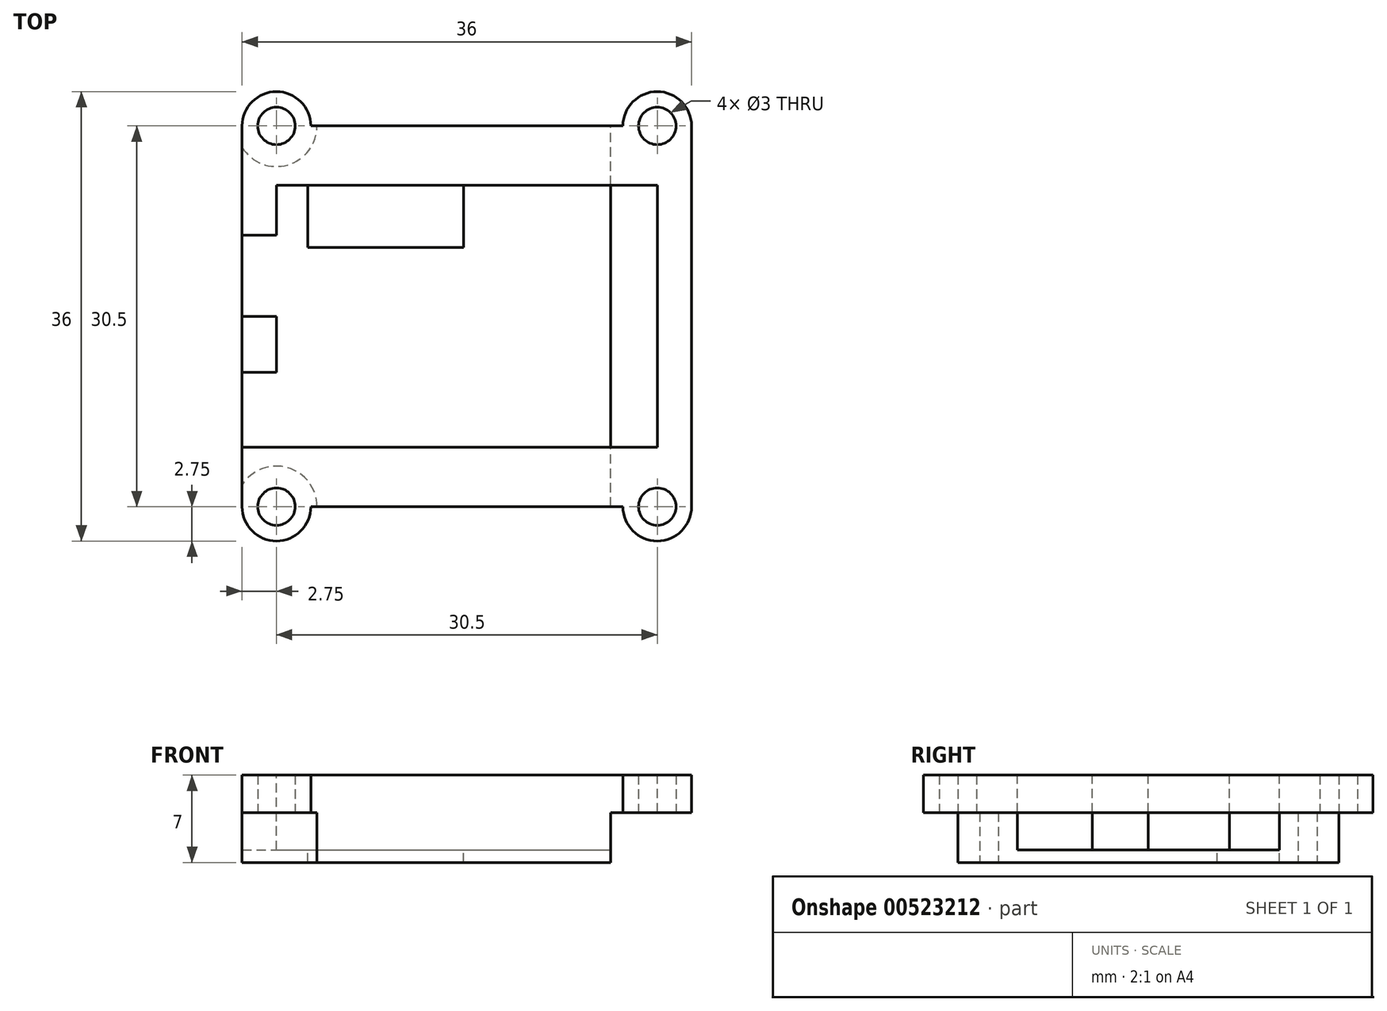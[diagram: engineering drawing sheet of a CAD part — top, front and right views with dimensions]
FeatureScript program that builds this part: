
annotation { "Feature Type Name" : "Feature", "Feature Type Description" : "" }
export const myFeature = defineFeature(function(context is Context, id is Id, definition is map)
    precondition{}
    {
        {
            var Q0;
            Q0=qCreatedBy(makeId("Top.planeOp"),FACE);
            var sketch = newSketch(context, id + "F0", { "sketchPlane" : qUnion([Q0])});
            skLineSegment(sketch, "E0.bottom", {"start": v(-18, -18) * mm, "end": v(18, -18) * mm});
            skLineSegment(sketch, "E0.top", {"start": v(-18, 18) * mm, "end": v(18, 18) * mm});
            skLineSegment(sketch, "E0.left", {"start": v(-18, -18) * mm, "end": v(-18, 18) * mm});
            skLineSegment(sketch, "E0.right", {"start": v(18, -18) * mm, "end": v(18, 18) * mm});
            skPoint(sketch, "E0.middle", {"position": v(0, 0) * mm});
            skSolve(sketch);
        }
        {
            var Q0;
            Q0=makeQuery(id+"F0.imprint","IMPRINT",FACE,{"disambiguationData":[TD([[makeQuery(id+"F0.imprint","IMPRINT",EDGE,{"derivedFrom":sQuery(id+"F0.wireOp",EDGE,"E0.bottom")}),1.0]])]});
            var Q1;
            Q1 = qSketchRegion(id + "F2", true);
            extrude(context, id + "F1", {"entities" : qUnion([Q0, Q1]), "depth" : 7 * mm, "offsetDistance" : 25 * mm});
        }
        {
            var Q0;
            Q0=makeQuery(id+"F1.opExtrude","CAP_FACE",FACE,{"disambiguationData":[OSD([sQuery(id+"F0.wireOp",EDGE,"E0.bottom"),sQuery(id+"F0.wireOp",EDGE,"E0.top"),sQuery(id+"F0.wireOp",EDGE,"E0.left"),sQuery(id+"F0.wireOp",EDGE,"E0.right")])],"isStart":false});
            var Q1;
            Q1=makeQuery(id+"F1.opExtrude","CAP_FACE",FACE,{"disambiguationData":[OSD([sQuery(id+"F0.wireOp",EDGE,"E0.bottom"),sQuery(id+"F0.wireOp",EDGE,"E0.top"),sQuery(id+"F0.wireOp",EDGE,"E0.left"),sQuery(id+"F0.wireOp",EDGE,"E0.right")])],"isStart":false});
            var Q2;
            Q2=makeQuery(id+"F1.opExtrude","CAP_FACE",FACE,{"disambiguationData":[OSD([sQuery(id+"F0.wireOp",EDGE,"E0.bottom"),sQuery(id+"F0.wireOp",EDGE,"E0.top"),sQuery(id+"F0.wireOp",EDGE,"E0.left"),sQuery(id+"F0.wireOp",EDGE,"E0.right")])],"isStart":false});
            var Q3;
            Q3=makeQuery(id+"F1.opExtrude","CAP_FACE",FACE,{"disambiguationData":[OSD([sQuery(id+"F0.wireOp",EDGE,"E0.bottom"),sQuery(id+"F0.wireOp",EDGE,"E0.top"),sQuery(id+"F0.wireOp",EDGE,"E0.left"),sQuery(id+"F0.wireOp",EDGE,"E0.right")])],"isStart":false});
            var Q4;
            Q4=makeQuery(id+"F1.opExtrude","CAP_FACE",FACE,{"disambiguationData":[OSD([sQuery(id+"F0.wireOp",EDGE,"E0.bottom"),sQuery(id+"F0.wireOp",EDGE,"E0.top"),sQuery(id+"F0.wireOp",EDGE,"E0.left"),sQuery(id+"F0.wireOp",EDGE,"E0.right")])],"isStart":false});
            var Q5;
            Q5=makeQuery(id+"F1.opExtrude","CAP_FACE",FACE,{"disambiguationData":[OSD([sQuery(id+"F0.wireOp",EDGE,"E0.bottom"),sQuery(id+"F0.wireOp",EDGE,"E0.top"),sQuery(id+"F0.wireOp",EDGE,"E0.left"),sQuery(id+"F0.wireOp",EDGE,"E0.right")])],"isStart":false});
            var Q6;
            Q6=makeQuery(id+"F1.opExtrude","CAP_FACE",FACE,{"disambiguationData":[OSD([sQuery(id+"F0.wireOp",EDGE,"E0.bottom"),sQuery(id+"F0.wireOp",EDGE,"E0.top"),sQuery(id+"F0.wireOp",EDGE,"E0.left"),sQuery(id+"F0.wireOp",EDGE,"E0.right")])],"isStart":false});
            var Q7;
            Q7=makeQuery(id+"F1.opExtrude","CAP_FACE",FACE,{"disambiguationData":[OSD([sQuery(id+"F0.wireOp",EDGE,"E0.bottom"),sQuery(id+"F0.wireOp",EDGE,"E0.top"),sQuery(id+"F0.wireOp",EDGE,"E0.left"),sQuery(id+"F0.wireOp",EDGE,"E0.right")])],"isStart":false});
            var sketch = newSketch(context, id + "F2", { "sketchPlane" : qUnion([Q0, Q1, Q2, Q3, Q4, Q5, Q6, Q7])});
            skLineSegment(sketch, "E1.bottom", {"start": v(-15.25, -10.5) * mm, "end": v(15.25, -10.5) * mm});
            skLineSegment(sketch, "E1.top", {"start": v(-15.25, 10.5) * mm, "end": v(15.25, 10.5) * mm});
            skLineSegment(sketch, "E1.left", {"start": v(-15.25, -10.5) * mm, "end": v(-15.25, 10.5) * mm});
            skLineSegment(sketch, "E1.right", {"start": v(15.25, -10.5) * mm, "end": v(15.25, 10.5) * mm});
            skPoint(sketch, "E1.middle", {"position": v(0, 0) * mm});
            skSolve(sketch);
        }
        {
            var Q0;
            Q0 = qSketchRegion(id + "F2", true);
            extrude(context, id + "F3", {"entities" : qUnion([Q0]), "operationType" : NewBodyOperationType.REMOVE, "oppositeDirection" : true, "depth" : 6 * mm, "offsetDistance" : 25 * mm});
        }
        {
            var Q0;
            Q0=makeQuery(id+"F2.imprint","IMPRINT",FACE,{"disambiguationData":[TD([[makeQuery(id+"F2.imprint","IMPRINT",EDGE,{"derivedFrom":sQuery(id+"F2.wireOp",EDGE,"E1.bottom")}),-1.0]])]});
            var Q1;
            Q1=makeQuery(id+"F2.imprint","IMPRINT",FACE,{"disambiguationData":[TD([[makeQuery(id+"F2.imprint","IMPRINT",EDGE,{"derivedFrom":sQuery(id+"F2.wireOp",EDGE,"E1.bottom")}),-1.0]])]});
            var sketch = newSketch(context, id + "F4", { "sketchPlane" : qUnion([Q0, Q1])});
            skLineSegment(sketch, "E2.bottom", {"start": v(-15.25, -10.5) * mm, "end": v(-18, -10.5) * mm});
            skLineSegment(sketch, "E2.top", {"start": v(-15.25, -4.5) * mm, "end": v(-18, -4.5) * mm});
            skLineSegment(sketch, "E2.left", {"start": v(-15.25, -10.5) * mm, "end": v(-15.25, -4.5) * mm});
            skLineSegment(sketch, "E2.right", {"start": v(-18, -10.5) * mm, "end": v(-18, -4.5) * mm});
            skSolve(sketch);
        }
        {
            var Q0;
            Q0 = qSketchRegion(id + "F4", true);
            extrude(context, id + "F5", {"entities" : qUnion([Q0]), "operationType" : NewBodyOperationType.REMOVE, "oppositeDirection" : true, "depth" : 6 * mm, "offsetDistance" : 25 * mm});
        }
        {
            var Q0;
            Q0=makeQuery(id+"F2.imprint","IMPRINT",FACE,{"disambiguationData":[TD([[makeQuery(id+"F2.imprint","IMPRINT",EDGE,{"derivedFrom":sQuery(id+"F2.wireOp",EDGE,"E1.bottom")}),-1.0]])]});
            var sketch = newSketch(context, id + "F6", { "sketchPlane" : qUnion([Q0])});
            skLineSegment(sketch, "E3.bottom", {"start": v(-18, 0) * mm, "end": v(-15.25, 0) * mm});
            skLineSegment(sketch, "E3.top", {"start": v(-18, 6.5) * mm, "end": v(-15.25, 6.5) * mm});
            skLineSegment(sketch, "E3.left", {"start": v(-18, 0) * mm, "end": v(-18, 6.5) * mm});
            skLineSegment(sketch, "E3.right", {"start": v(-15.25, 0) * mm, "end": v(-15.25, 6.5) * mm});
            skSolve(sketch);
        }
        {
            var Q0;
            Q0 = qSketchRegion(id + "F6", true);
            extrude(context, id + "F7", {"entities" : qUnion([Q0]), "operationType" : NewBodyOperationType.REMOVE, "oppositeDirection" : true, "depth" : 6 * mm, "offsetDistance" : 25 * mm});
        }
        {
            var Q0;
            Q0=makeQuery(id+"F2.imprint","IMPRINT",FACE,{"disambiguationData":[TD([[makeQuery(id+"F2.imprint","IMPRINT",EDGE,{"derivedFrom":sQuery(id+"F2.wireOp",EDGE,"E1.bottom")}),1.0]])]});
            var Q1;
            Q1=qCreatedBy(makeId("Top.planeOp"),FACE);
            var sketch = newSketch(context, id + "F8", { "sketchPlane" : qUnion([Q0, Q1])});
            skLineSegment(sketch, "E4.bottom", {"start": v(-12.75, 10.5) * mm, "end": v(-0.25, 10.5) * mm});
            skLineSegment(sketch, "E4.top", {"start": v(-12.75, 5.5) * mm, "end": v(-0.25, 5.5) * mm});
            skLineSegment(sketch, "E4.left", {"start": v(-12.75, 10.5) * mm, "end": v(-12.75, 5.5) * mm});
            skLineSegment(sketch, "E4.right", {"start": v(-0.25, 10.5) * mm, "end": v(-0.25, 5.5) * mm});
            skSolve(sketch);
        }
        {
            var Q0;
            Q0 = qSketchRegion(id + "F8", true);
            extrude(context, id + "F9", {"entities" : qUnion([Q0]), "operationType" : NewBodyOperationType.REMOVE, "oppositeDirection" : true, "depth" : 7 * mm, "offsetDistance" : 25 * mm});
        }
        {
            var Q0;
            Q0=qCreatedBy(makeId("Top.planeOp"),FACE);
            var Q1;
            Q1=qCreatedBy(makeId("Top.planeOp"),FACE);
            var Q2;
            Q2=qCreatedBy(makeId("Top.planeOp"),FACE);
            var Q3;
            Q3=qCreatedBy(makeId("Top.planeOp"),FACE);
            var Q4;
            Q4=qCreatedBy(makeId("Top.planeOp"),FACE);
            var Q5;
            Q5=makeQuery(id+"F2.imprint","IMPRINT",FACE,{"disambiguationData":[TD([[makeQuery(id+"F2.imprint","IMPRINT",EDGE,{"derivedFrom":sQuery(id+"F2.wireOp",EDGE,"E1.bottom")}),-1.0]])]});
            var sketch = newSketch(context, id + "F10", { "sketchPlane" : qUnion([Q0, Q1, Q2, Q3, Q4, Q5])});
            skLineSegment(sketch, "E5.bottom", {"start": v(-15.25, 15.25) * mm, "end": v(15.25, 15.25) * mm});
            skLineSegment(sketch, "E5.left", {"start": v(-15.25, 15.25) * mm, "end": v(-15.25, -15.25) * mm});
            skLineSegment(sketch, "E5.right", {"start": v(15.25, 15.25) * mm, "end": v(15.25, -15.25) * mm});
            skPoint(sketch, "E5.middle", {"position": v(0, 0) * mm});
            skCircle(sketch, "E6", {"center": v(-15.25, 15.25) * mm, "radius": 2.75 * mm});
            skCircle(sketch, "E7", {"center": v(15.25, 15.25) * mm, "radius": 2.75 * mm});
            skCircle(sketch, "E8", {"center": v(15.25, -15.25) * mm, "radius": 2.75 * mm});
            skCircle(sketch, "E9", {"center": v(-15.25, -15.25) * mm, "radius": 2.75 * mm});
            skArc(sketch, "E10", {"start": v(-15.25, 18) * mm, "mid": v(-13.3, 17.2) * mm, "end": v(-12.5, 15.25) * mm});
            skArc(sketch, "E11", {"start": v(-15.25, 18) * mm, "mid": v(-17.2, 17.2) * mm, "end": v(-18, 15.25) * mm});
            skArc(sketch, "E12", {"start": v(15.25, 18) * mm, "mid": v(13.3, 17.2) * mm, "end": v(12.5, 15.25) * mm});
            skArc(sketch, "E13", {"start": v(15.25, 18) * mm, "mid": v(17.2, 17.2) * mm, "end": v(18, 15.25) * mm});
            skArc(sketch, "E14", {"start": v(-15.25, -18) * mm, "mid": v(-17.2, -17.2) * mm, "end": v(-18, -15.25) * mm});
            skArc(sketch, "E15", {"start": v(-12.5, -15.25) * mm, "mid": v(-13.3, -17.2) * mm, "end": v(-15.25, -18) * mm});
            skArc(sketch, "E16", {"start": v(12.54, -15.74) * mm, "mid": v(13.49, -17.36) * mm, "end": v(15.25, -18) * mm});
            skArc(sketch, "E17", {"start": v(18, -15.25) * mm, "mid": v(17.2, -17.2) * mm, "end": v(15.25, -18) * mm});
            skLineSegment(sketch, "E18", {"start": v(-12.5, -15.25) * mm, "end": v(12.54, -15.74) * mm});
            skLineSegment(sketch, "E19", {"start": v(-15.25, -18) * mm, "end": v(15.25, -18) * mm});
            skSolve(sketch);
        }
        {
            var Q0;
            Q0=sQuery(id+"F10.wireOp",VERTEX,"E5.bottom.start");
            var Q1;
            Q1=sQuery(id+"F10.wireOp",VERTEX,"E5.bottom.end");
            var Q2;
            Q2=sQuery(id+"F10.wireOp",VERTEX,"E5.left.end");
            var Q3;
            Q3=sQuery(id+"F10.wireOp",VERTEX,"E5.right.end");
            var Q4;
            Q4=makeQuery(id+"F1.opExtrude","SWEPT_BODY",BODY,{"disambiguationData":[OSD([sQuery(id+"F0.wireOp",EDGE,"E0.bottom"),sQuery(id+"F0.wireOp",EDGE,"E0.top"),sQuery(id+"F0.wireOp",EDGE,"E0.left"),sQuery(id+"F0.wireOp",EDGE,"E0.right")])]});
            hole(context, id + "F11", {"style" : HoleStyle.SIMPLE, "endStyle" : HoleEndStyle.THROUGH, "oppositeDirection" : true, "holeDiameter" : 3 * mm, "isTappedThrough" : true, "tappedDepth" : 12 * mm, "tapClearance" : 3, "locations" : qUnion([Q0, Q1, Q2, Q3]), "scope" : qUnion([Q4])});
        }
        {
            var Q0;
            Q0=qCreatedBy(makeId("Top.planeOp"),FACE);
            var sketch = newSketch(context, id + "F12", { "sketchPlane" : qUnion([Q0])});
            skArc(sketch, "E20", {"start": v(-15.25, 18) * mm, "mid": v(-13.3, 17.2) * mm, "end": v(-12.5, 15.25) * mm});
            skArc(sketch, "E21", {"start": v(15.25, 18) * mm, "mid": v(17.2, 17.2) * mm, "end": v(18, 15.25) * mm});
            skArc(sketch, "E22", {"start": v(18, -15.25) * mm, "mid": v(17.2, -17.2) * mm, "end": v(15.25, -18) * mm});
            skArc(sketch, "E23", {"start": v(-15.25, -18) * mm, "mid": v(-17.2, -17.2) * mm, "end": v(-18, -15.25) * mm});
            skArc(sketch, "E24", {"start": v(-15.25, 18) * mm, "mid": v(-17.2, 17.2) * mm, "end": v(-18, 15.25) * mm});
            skArc(sketch, "E25", {"start": v(15.25, 18) * mm, "mid": v(13.3, 17.2) * mm, "end": v(12.5, 15.25) * mm});
            skArc(sketch, "E26", {"start": v(-15.25, -18) * mm, "mid": v(-13.3, -17.2) * mm, "end": v(-12.5, -15.25) * mm});
            skArc(sketch, "E27", {"start": v(15.25, -18) * mm, "mid": v(13.3, -17.2) * mm, "end": v(12.5, -15.25) * mm});
            skLineSegment(sketch, "E28", {"start": v(-12.5, -15.25) * mm, "end": v(12.5, -15.25) * mm});
            skLineSegment(sketch, "E29", {"start": v(-15.25, -18) * mm, "end": v(15.25, -18) * mm});
            skLineSegment(sketch, "E30", {"start": v(-12.5, 15.25) * mm, "end": v(12.5, 15.25) * mm});
            skLineSegment(sketch, "E31", {"start": v(-15.25, 18) * mm, "end": v(15.25, 18) * mm});
            skLineSegment(sketch, "E32", {"start": v(-15.25, 18) * mm, "end": v(-18.01, 18) * mm});
            skLineSegment(sketch, "E33", {"start": v(-18.01, 18) * mm, "end": v(-18, 15.25) * mm});
            skLineSegment(sketch, "E34", {"start": v(15.25, 18) * mm, "end": v(18, 18) * mm});
            skLineSegment(sketch, "E35", {"start": v(18, 18) * mm, "end": v(18, 15.25) * mm});
            skLineSegment(sketch, "E36", {"start": v(-18, -15.25) * mm, "end": v(-18, -18) * mm});
            skLineSegment(sketch, "E37", {"start": v(-18, -18) * mm, "end": v(-15.25, -18) * mm});
            skLineSegment(sketch, "E38", {"start": v(15.25, -18) * mm, "end": v(18, -18) * mm});
            skLineSegment(sketch, "E39", {"start": v(18, -18) * mm, "end": v(18, -15.25) * mm});
            skSolve(sketch);
        }
        {
            var Q0;
            Q0 = qSketchRegion(id + "F12", true);
            var Q1;
            Q1 = qSketchRegion(id + "F12", true);
            extrude(context, id + "F13", {"entities" : qUnion([Q0, Q1]), "operationType" : NewBodyOperationType.REMOVE, "depth" : 25 * mm, "offsetDistance" : 25 * mm});
        }
        {
            var Q0;
            Q0=qCreatedBy(makeId("Top.planeOp"),FACE);
            var Q1;
            Q1=qCreatedBy(makeId("Top.planeOp"),FACE);
            var Q2;
            Q2=qCreatedBy(makeId("Top.planeOp"),FACE);
            var sketch = newSketch(context, id + "F14", { "sketchPlane" : qUnion([Q0, Q1, Q2])});
            skCircle(sketch, "E40", {"center": v(-15.25, -15.25) * mm, "radius": 3.25 * mm});
            skCircle(sketch, "E41", {"center": v(15.25, -15.25) * mm, "radius": 3.25 * mm});
            skCircle(sketch, "E42", {"center": v(-15.25, 15.25) * mm, "radius": 3.25 * mm});
            skCircle(sketch, "E43", {"center": v(15.25, 15.25) * mm, "radius": 3.25 * mm});
            skSolve(sketch);
        }
        {
            var Q0;
            Q0 = qSketchRegion(id + "F14", true);
            extrude(context, id + "F15", {"entities" : qUnion([Q0]), "operationType" : NewBodyOperationType.REMOVE, "depth" : 4 * mm, "offsetDistance" : 25 * mm});
        }
        {
            var Q0;
            Q0=qCreatedBy(makeId("Top.planeOp"),FACE);
            var Q1;
            Q1=qCreatedBy(makeId("Top.planeOp"),FACE);
            var sketch = newSketch(context, id + "F16", { "sketchPlane" : qUnion([Q0, Q1])});
            skLineSegment(sketch, "E44.bottom", {"start": v(18, -18) * mm, "end": v(11.5, -18) * mm});
            skLineSegment(sketch, "E44.top", {"start": v(18, 18) * mm, "end": v(11.5, 18) * mm});
            skLineSegment(sketch, "E44.left", {"start": v(18, -18) * mm, "end": v(18, 18) * mm});
            skLineSegment(sketch, "E44.right", {"start": v(11.5, -18) * mm, "end": v(11.5, 18) * mm});
            skSolve(sketch);
        }
        {
            var Q0;
            Q0 = qSketchRegion(id + "F16", true);
            extrude(context, id + "F17", {"entities" : qUnion([Q0]), "operationType" : NewBodyOperationType.REMOVE, "depth" : 4 * mm, "offsetDistance" : 25 * mm});
        }
    });
